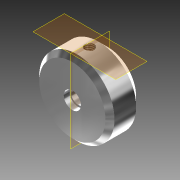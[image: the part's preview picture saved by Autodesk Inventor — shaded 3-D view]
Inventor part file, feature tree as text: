
AUTODESK INVENTOR PART (.ipt)
format: ipt  version: 2015 (Build 190159000, 159)  size: 126,464 bytes
history: native  units: mm
features: revolve x2, chamfer x2, hole x2, plane x1
ambient origin geometry x8: Origin, YZ Plane, XZ Plane, XY Plane, X Axis, Y Axis, Z Axis, Center Point
bodies: Solid1 (feature_tree)
feature tree (7):
  revolve  "Revolución1"  [1 undecoded]
  revolve  "Revolución2"  [1 undecoded]
  chamfer  "Chaflán1"  Distance=7.0mm
  plane  "Plano de trabajo1"
  hole  "Agujero2"  [1 undecoded]
  chamfer  "Chaflán2"  Angle=90.0deg  [1 undecoded]
  hole  "Agujero3"  [1 undecoded]
note: 5 required parameter values undecoded (feature->parameter linkage not recoverable at this tier; creation-order binding heuristic only, values carry confidence <= 0.55)